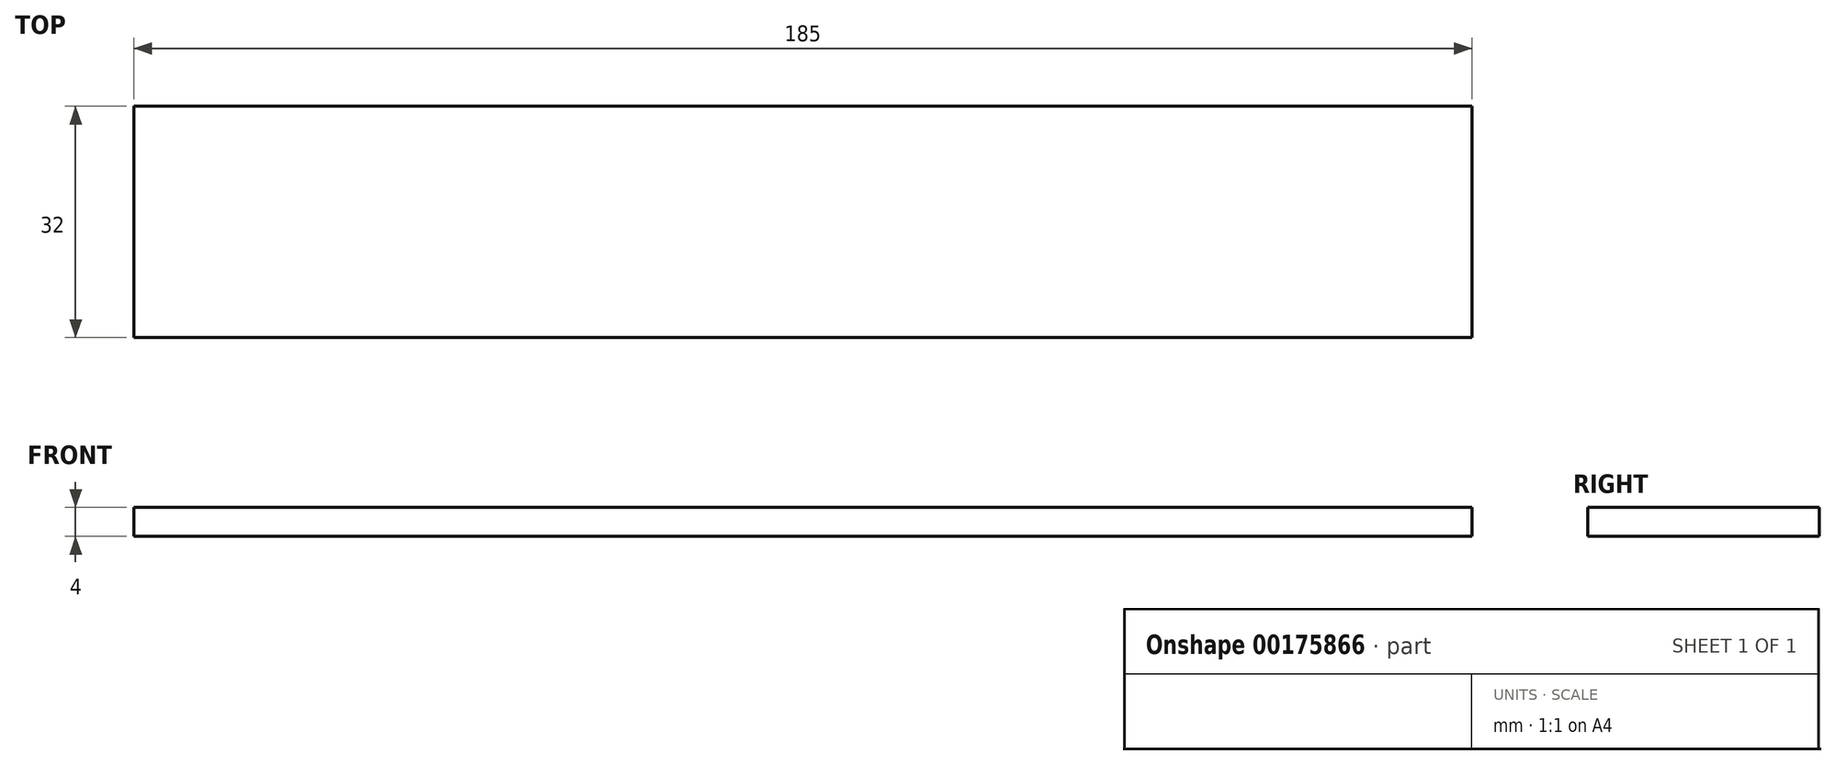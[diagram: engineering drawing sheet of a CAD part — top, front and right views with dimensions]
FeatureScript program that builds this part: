
annotation { "Feature Type Name" : "Feature", "Feature Type Description" : "" }
export const myFeature = defineFeature(function(context is Context, id is Id, definition is map)
    precondition{}
    {
        {
            var Q0;
            Q0=qCreatedBy(makeId("Top.planeOp"),FACE);
            var sketch = newSketch(context, id + "F0", { "sketchPlane" : qUnion([Q0])});
            skLineSegment(sketch, "E0.bottom", {"start": v(-120.49, -3.6) * mm, "end": v(64.51, -3.6) * mm});
            skLineSegment(sketch, "E0.top", {"start": v(-120.49, -35.6) * mm, "end": v(64.51, -35.6) * mm});
            skLineSegment(sketch, "E0.left", {"start": v(-120.49, -3.6) * mm, "end": v(-120.49, -35.6) * mm});
            skLineSegment(sketch, "E0.right", {"start": v(64.51, -3.6) * mm, "end": v(64.51, -35.6) * mm});
            skSolve(sketch);
        }
        {
            var Q0;
            Q0=qSketchRegion(id+"F0",true);
            extrude(context, id + "F1", {"entities" : qUnion([Q0]), "depth" : 4 * mm});
        }
    });
